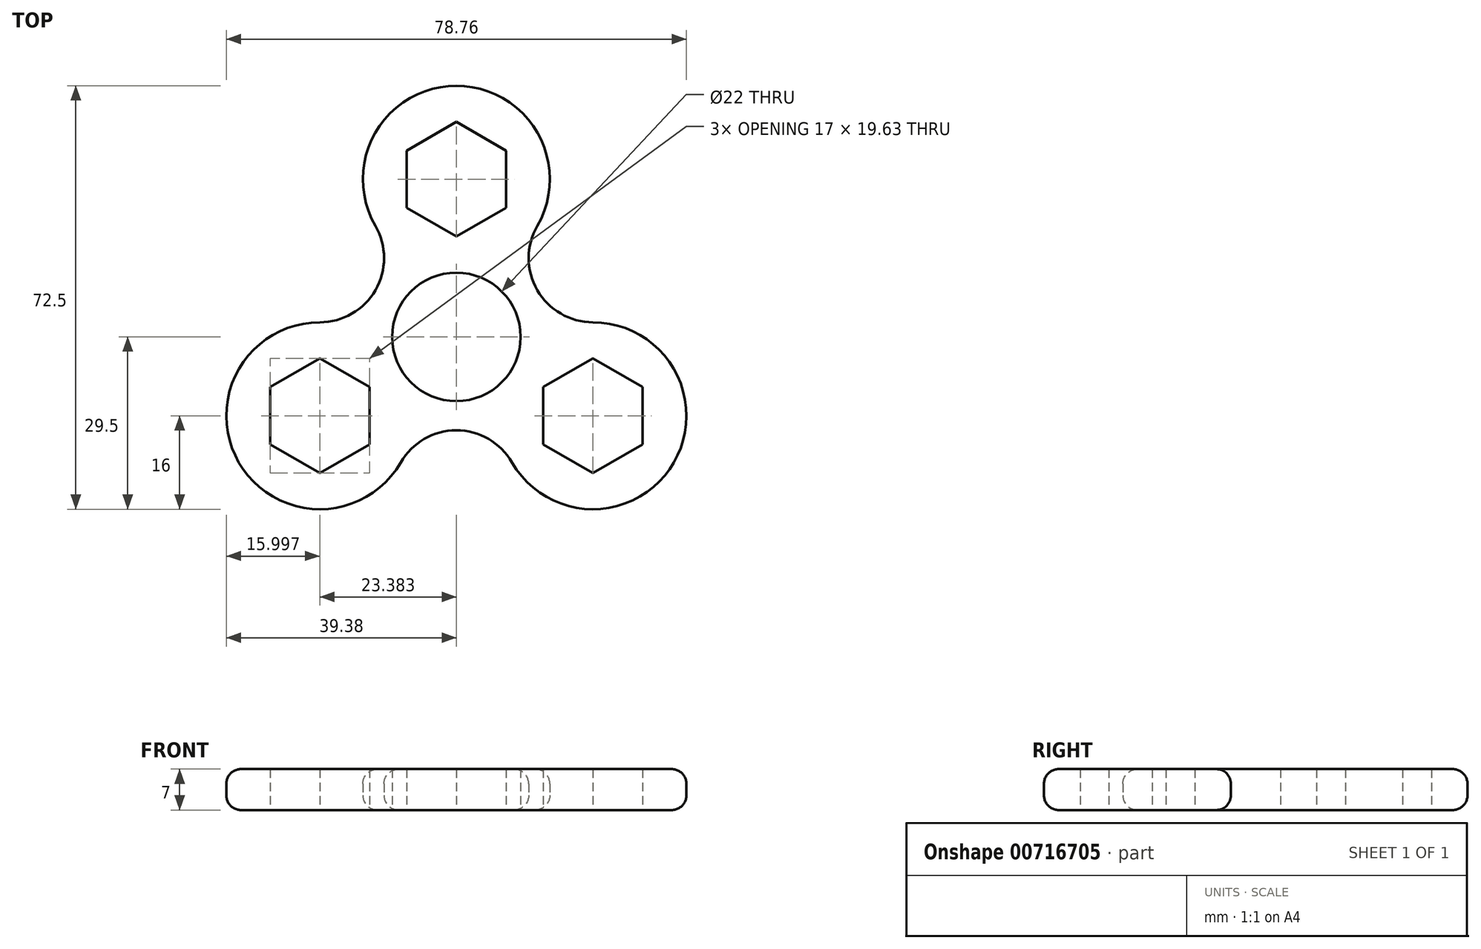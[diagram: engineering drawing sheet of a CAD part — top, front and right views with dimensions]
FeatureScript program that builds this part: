
annotation { "Feature Type Name" : "Feature", "Feature Type Description" : "" }
export const myFeature = defineFeature(function(context is Context, id is Id, definition is map)
    precondition{}
    {
        {
            var Q0;
            Q0=qCreatedBy(makeId("Top.planeOp"),FACE);
            var sketch = newSketch(context, id + "F0", { "sketchPlane" : qUnion([Q0])});
            skCircle(sketch, "E0", {"center": v(0, 0) * mm, "radius": 11 * mm});
            skLineSegment(sketch, "E1", {"start": v(0, 0) * mm, "end": v(-39.98, 23.08) * mm, "construction": true});
            skLineSegment(sketch, "E2.MirrorCS", {"start": v(0, 0) * mm, "end": v(39.98, 23.08) * mm, "construction": true});
            skLineSegment(sketch, "E3", {"start": v(0, 0) * mm, "end": v(0, -50.92) * mm, "construction": true});
            skCircle(sketch, "E4", {"center": v(-23.38, 13.5) * mm, "radius": 11 * mm});
            skCircle(sketch, "E5.MirrorC", {"center": v(23.38, 13.5) * mm, "radius": 11 * mm});
            skLineSegment(sketch, "E6.MirrorCS", {"start": v(0, 0) * mm, "end": v(39.98, -23.08) * mm, "construction": true});
            skCircle(sketch, "E7.MirrorC", {"center": v(0, -27) * mm, "radius": 11 * mm});
            skCircle(sketch, "E8", {"center": v(0, 27) * mm, "radius": 16 * mm});
            skCircle(sketch, "E9.MirrorC", {"center": v(23.38, -13.5) * mm, "radius": 16 * mm});
            skCircle(sketch, "E10.MirrorC", {"center": v(-23.38, -13.5) * mm, "radius": 16 * mm});
            skCircle(sketch, "E11.cCircle", {"center": v(0, 27) * mm, "radius": 8.5 * mm, "construction": true});
            skLineSegment(sketch, "E11.0", {"start": v(8.5, 31.9) * mm, "end": v(8.5, 22.1) * mm});
            skLineSegment(sketch, "E11.1", {"start": v(8.5, 22.1) * mm, "end": v(0, 17.19) * mm});
            skLineSegment(sketch, "E11.2", {"start": v(0, 17.19) * mm, "end": v(-8.5, 22.1) * mm});
            skLineSegment(sketch, "E11.3", {"start": v(-8.5, 22.1) * mm, "end": v(-8.5, 31.9) * mm});
            skLineSegment(sketch, "E11.4", {"start": v(-8.5, 31.9) * mm, "end": v(0, 36.81) * mm});
            skLineSegment(sketch, "E11.5", {"start": v(0, 36.81) * mm, "end": v(8.5, 31.9) * mm});
            skPoint(sketch, "E11.0.midPoint", {"position": v(8.5, 27) * mm});
            skLineSegment(sketch, "E12.MirrorCS", {"start": v(-14.88, -8.6) * mm, "end": v(-23.38, -3.69) * mm});
            skLineSegment(sketch, "E13.MirrorCS", {"start": v(-23.38, -3.69) * mm, "end": v(-31.88, -8.6) * mm});
            skLineSegment(sketch, "E14.MirrorCS", {"start": v(-31.88, -8.6) * mm, "end": v(-31.88, -18.4) * mm});
            skLineSegment(sketch, "E15.MirrorCS", {"start": v(-31.88, -18.4) * mm, "end": v(-23.38, -23.31) * mm});
            skLineSegment(sketch, "E16.MirrorCS", {"start": v(-23.38, -23.31) * mm, "end": v(-14.88, -18.4) * mm});
            skLineSegment(sketch, "E17.MirrorCS", {"start": v(-14.88, -18.4) * mm, "end": v(-14.88, -8.6) * mm});
            skLineSegment(sketch, "E18.MirrorCS", {"start": v(23.38, -3.69) * mm, "end": v(14.88, -8.6) * mm});
            skLineSegment(sketch, "E19.MirrorCS", {"start": v(14.88, -8.6) * mm, "end": v(14.88, -18.4) * mm});
            skLineSegment(sketch, "E20.MirrorCS", {"start": v(14.88, -18.4) * mm, "end": v(23.38, -23.31) * mm});
            skLineSegment(sketch, "E21.MirrorCS", {"start": v(23.38, -23.31) * mm, "end": v(31.88, -18.4) * mm});
            skLineSegment(sketch, "E22.MirrorCS", {"start": v(31.88, -18.4) * mm, "end": v(31.88, -8.6) * mm});
            skLineSegment(sketch, "E23.MirrorCS", {"start": v(31.88, -8.6) * mm, "end": v(23.38, -3.69) * mm});
            skSolve(sketch);
        }
        {
            var Q0;
            {var subQ0=sQuery(id+"F0.wireOp",EDGE,"E10.MirrorC");var subQ1=sQuery(id+"F0.wireOp",EDGE,"E0");var subQ2=makeQuery(id+"F0.imprint","INTERSECT",VERTEX,{"derivedFrom":[subQ1,subQ0]});Q0=makeQuery(id+"F0.imprint","IMPRINT",FACE,{"disambiguationData":[TD([[makeQuery(id+"F0.imprint","IMPRINT",EDGE,{"disambiguationData":[TD([[subQ2,1.0]])],"derivedFrom":subQ1}),-1.0]])]});}
            var Q1;
            Q1=makeQuery(id+"F0.imprint","IMPRINT",FACE,{"disambiguationData":[TD([[makeQuery(id+"F0.imprint","IMPRINT",EDGE,{"derivedFrom":sQuery(id+"F0.wireOp",EDGE,"E11.0")}),1.0]])]});
            var Q2;
            {var subQ0=sQuery(id+"F0.wireOp",EDGE,"E8");var subQ1=sQuery(id+"F0.wireOp",EDGE,"E0");var subQ2=makeQuery(id+"F0.imprint","INTERSECT",VERTEX,{"derivedFrom":[subQ1,subQ0]});Q2=makeQuery(id+"F0.imprint","IMPRINT",FACE,{"disambiguationData":[TD([[makeQuery(id+"F0.imprint","IMPRINT",EDGE,{"disambiguationData":[TD([[subQ2,1.0]])],"derivedFrom":subQ1}),-1.0]])]});}
            var Q3;
            Q3=makeQuery(id+"F0.imprint","IMPRINT",FACE,{"disambiguationData":[TD([[makeQuery(id+"F0.imprint","IMPRINT",EDGE,{"derivedFrom":sQuery(id+"F0.wireOp",EDGE,"E18.MirrorCS")}),-1.0]])]});
            var Q4;
            {var subQ0=sQuery(id+"F0.wireOp",EDGE,"E10.MirrorC");var subQ1=sQuery(id+"F0.wireOp",EDGE,"E0");var subQ2=makeQuery(id+"F0.imprint","INTERSECT",VERTEX,{"derivedFrom":[subQ1,subQ0]});Q4=makeQuery(id+"F0.imprint","IMPRINT",FACE,{"disambiguationData":[TD([[makeQuery(id+"F0.imprint","IMPRINT",EDGE,{"disambiguationData":[TD([[subQ2,-1.0]])],"derivedFrom":subQ1}),-1.0]])]});}
            var Q5;
            Q5=makeQuery(id+"F0.imprint","IMPRINT",FACE,{"disambiguationData":[TD([[makeQuery(id+"F0.imprint","IMPRINT",EDGE,{"derivedFrom":sQuery(id+"F0.wireOp",EDGE,"E12.MirrorCS")}),-1.0]])]});
            extrude(context, id + "F1", {"entities" : qUnion([Q0, Q1, Q2, Q3, Q4, Q5]), "depth" : 7 * mm, "offsetDistance" : 25 * mm});
        }
        {
            var Q0;
            Q0=makeQuery(id+"F1.opExtrude","CAP_EDGE",EDGE,{"disambiguationData":[OSD([sQuery(id+"F0.wireOp",EDGE,"E8")])],"isStart":false});
            var Q1;
            Q1=makeQuery(id+"F1.opExtrude","CAP_EDGE",EDGE,{"disambiguationData":[OSD([sQuery(id+"F0.wireOp",EDGE,"E8")])],"isStart":true});
            var Q2;
            Q2=makeQuery(id+"F1.opExtrude","CAP_EDGE",EDGE,{"disambiguationData":[OSD([sQuery(id+"F0.wireOp",EDGE,"E5.MirrorC")])],"isStart":false});
            var Q3;
            Q3=makeQuery(id+"F1.opExtrude","CAP_EDGE",EDGE,{"disambiguationData":[OSD([sQuery(id+"F0.wireOp",EDGE,"E5.MirrorC")])],"isStart":true});
            var Q4;
            Q4=makeQuery(id+"F1.opExtrude","CAP_EDGE",EDGE,{"disambiguationData":[OSD([sQuery(id+"F0.wireOp",EDGE,"E9.MirrorC")])],"isStart":true});
            var Q5;
            Q5=makeQuery(id+"F1.opExtrude","CAP_EDGE",EDGE,{"disambiguationData":[OSD([sQuery(id+"F0.wireOp",EDGE,"E9.MirrorC")])],"isStart":false});
            var Q6;
            Q6=makeQuery(id+"F1.opExtrude","CAP_EDGE",EDGE,{"disambiguationData":[OSD([sQuery(id+"F0.wireOp",EDGE,"E7.MirrorC")])],"isStart":false});
            var Q7;
            Q7=makeQuery(id+"F1.opExtrude","CAP_EDGE",EDGE,{"disambiguationData":[OSD([sQuery(id+"F0.wireOp",EDGE,"E7.MirrorC")])],"isStart":true});
            var Q8;
            Q8=makeQuery(id+"F1.opExtrude","CAP_EDGE",EDGE,{"disambiguationData":[OSD([sQuery(id+"F0.wireOp",EDGE,"E10.MirrorC")])],"isStart":true});
            var Q9;
            Q9=makeQuery(id+"F1.opExtrude","CAP_EDGE",EDGE,{"disambiguationData":[OSD([sQuery(id+"F0.wireOp",EDGE,"E10.MirrorC")])],"isStart":false});
            var Q10;
            Q10=makeQuery(id+"F1.opExtrude","CAP_EDGE",EDGE,{"disambiguationData":[OSD([sQuery(id+"F0.wireOp",EDGE,"E4")])],"isStart":false});
            var Q11;
            Q11=makeQuery(id+"F1.opExtrude","CAP_EDGE",EDGE,{"disambiguationData":[OSD([sQuery(id+"F0.wireOp",EDGE,"E4")])],"isStart":true});
            fillet(context, id + "F2", {"entities" : qUnion([Q0, Q1, Q2, Q3, Q4, Q5, Q6, Q7, Q8, Q9, Q10, Q11]), "radius" : 2.5 * mm, "tangentPropagation" : true, "allowEdgeOverflow" : false});
        }
    });
